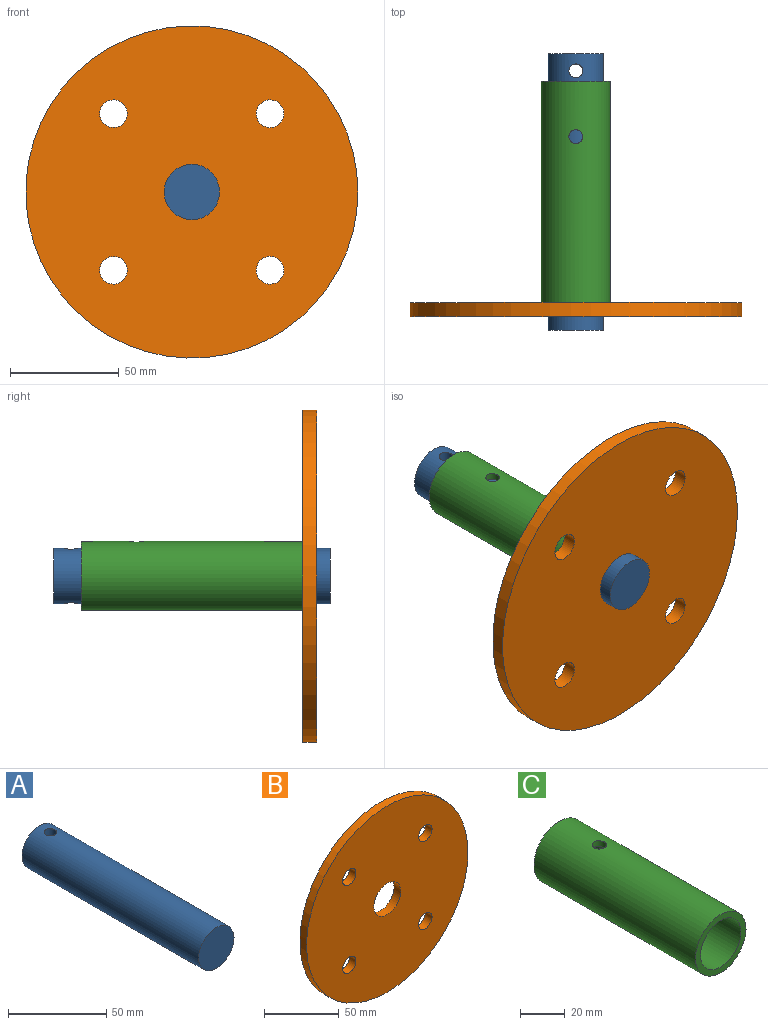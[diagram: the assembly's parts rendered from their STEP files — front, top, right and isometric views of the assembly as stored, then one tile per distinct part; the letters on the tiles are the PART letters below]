
ASSEMBLY  parts=3 mates=2
PART A: 4 faces, bbox 25.4x127x25.4 mm
  f0: cylinder r=12.7mm len=127mm, axis (0,1,0), area 10070.3mm2, adj f1,f2,f3
  f1: plane 25.4x25.4mm, normal (0,-1,0), area 506.7mm2, adj f0
  f2: plane 25.4x25.4mm, normal (0,1,0), area 506.7mm2, adj f0
  f3: cylinder r=3.17mm len=25.4mm, axis (0,0,1), area 498.7mm2, adj f0
PART B: 8 faces, bbox 152.4x6.4x152.4 mm
  f0: cylinder r=76.2mm len=152.4mm, axis (0,1,0), area 3040.2mm2, adj f6,f7
  f1: cylinder r=12.7mm len=25.4mm, axis (0,1,0), area 506.7mm2, adj f6,f7
  f2: cylinder r=6.35mm len=12.7mm, axis (0,1,0), area 253.4mm2, adj f6,f7
  f3: cylinder r=6.35mm len=12.7mm, axis (0,1,0), area 253.4mm2, adj f6,f7
  f4: cylinder r=6.35mm len=12.7mm, axis (0,1,0), area 253.4mm2, adj f6,f7
  f5: cylinder r=6.35mm len=12.7mm, axis (0,1,0), area 253.4mm2, adj f6,f7
  f6: plane 152.4x152.4mm, normal (0,-1,0), area 17228.1mm2, adj f0,f1,f2,f3,f4,f5
  f7: plane 152.4x152.4mm, normal (0,1,0), area 17228.1mm2, adj f0,f1,f2,f3,f4,f5
PART C: 5 faces, bbox 31.8x101.6x31.8 mm
  f0: cylinder r=12.7mm len=101.6mm, axis (0,1,0), area 8075.3mm2, adj f2,f3,f4
  f1: cylinder r=15.88mm len=101.6mm, axis (0,1,0), area 10102.1mm2, adj f2,f3,f4
  f2: plane 31.75x31.75mm, normal (0,-1,0), area 285mm2, adj f0,f1
  f3: plane 31.75x31.75mm, normal (0,1,0), area 285mm2, adj f0,f1
  f4: cylinder r=3.17mm len=6.35mm, axis (0,0,-1), area 64.2mm2, adj f0,f1
PLACE A t=(-39.8,34.61,-8.87)mm
PLACE B t=(-39.8,-79.69,-8.87)mm
PLACE C t=(-39.8,21.91,-8.87)mm fixed
MATE revolute C.f0 <-> A.f0  axis (0,1,0) through (-39.8,-28.89,-8.87)mm
MATE fastened B.f0 <-> A.f0  axis (0,-1,0) through (-39.8,-86.04,-8.87)mm
